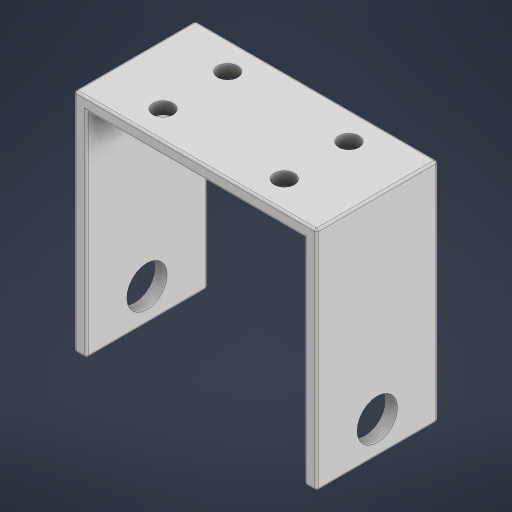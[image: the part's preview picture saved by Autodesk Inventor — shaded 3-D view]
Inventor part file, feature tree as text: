
AUTODESK INVENTOR PART (.ipt)
format: ipt  version: 2023 (Build 270158000, 158)  size: 229,376 bytes
history: native  units: mm
features: sketch x4, hole x3, extrude x1, fillet x1
ambient origin geometry x8: Origin, YZ Plane, XZ Plane, XY Plane, X Axis, Y Axis, Z Axis, Center Point
bodies: Solid1 (feature_tree)
feature tree (9):
  extrude  "Extrusion1"  Depth=56.0mm
  hole  "Hole1"  [1 undecoded]
  hole  "Hole2"  [1 undecoded]
  hole  "Hole3"  [1 undecoded]
  fillet  "Fillet1"  Radius=15.0mm
  sketch  "Sketch1"  dims[d2=3.0mm d4=56.0mm]
  sketch  "Sketch2"  dims[d5=53.0mm d6=30.0mm d7=0.0mm]
  sketch  "Sketch3"  dims[d8=45.0mm d9=15.0mm]
  sketch  "Sketch4"  dims[d10=10.0mm d11=6.0mm d12=4.0mm d13=2.0mm d14=90.0deg d15=8.0mm d16=20.594885mm d17=45.0mm d18=15.0mm d19=10.0mm d20=6.0mm d21=4.0mm d22=2.0mm d23=90.0deg d24=8.0mm d25=20.594885mm d26=7.0mm d27=15.0mm d28=7.0mm d29=15.0mm d30=7.0mm d31=15.0mm d32=15.0mm d33=7.0mm d34=5.0mm d35=6.0mm d36=4.0mm d37=2.0mm d38=90.0deg d39=8.0mm d40=20.594885mm d41=0.5mm]
note: 3 required parameter values undecoded (feature->parameter linkage not recoverable at this tier; creation-order binding heuristic only, values carry confidence <= 0.55)
